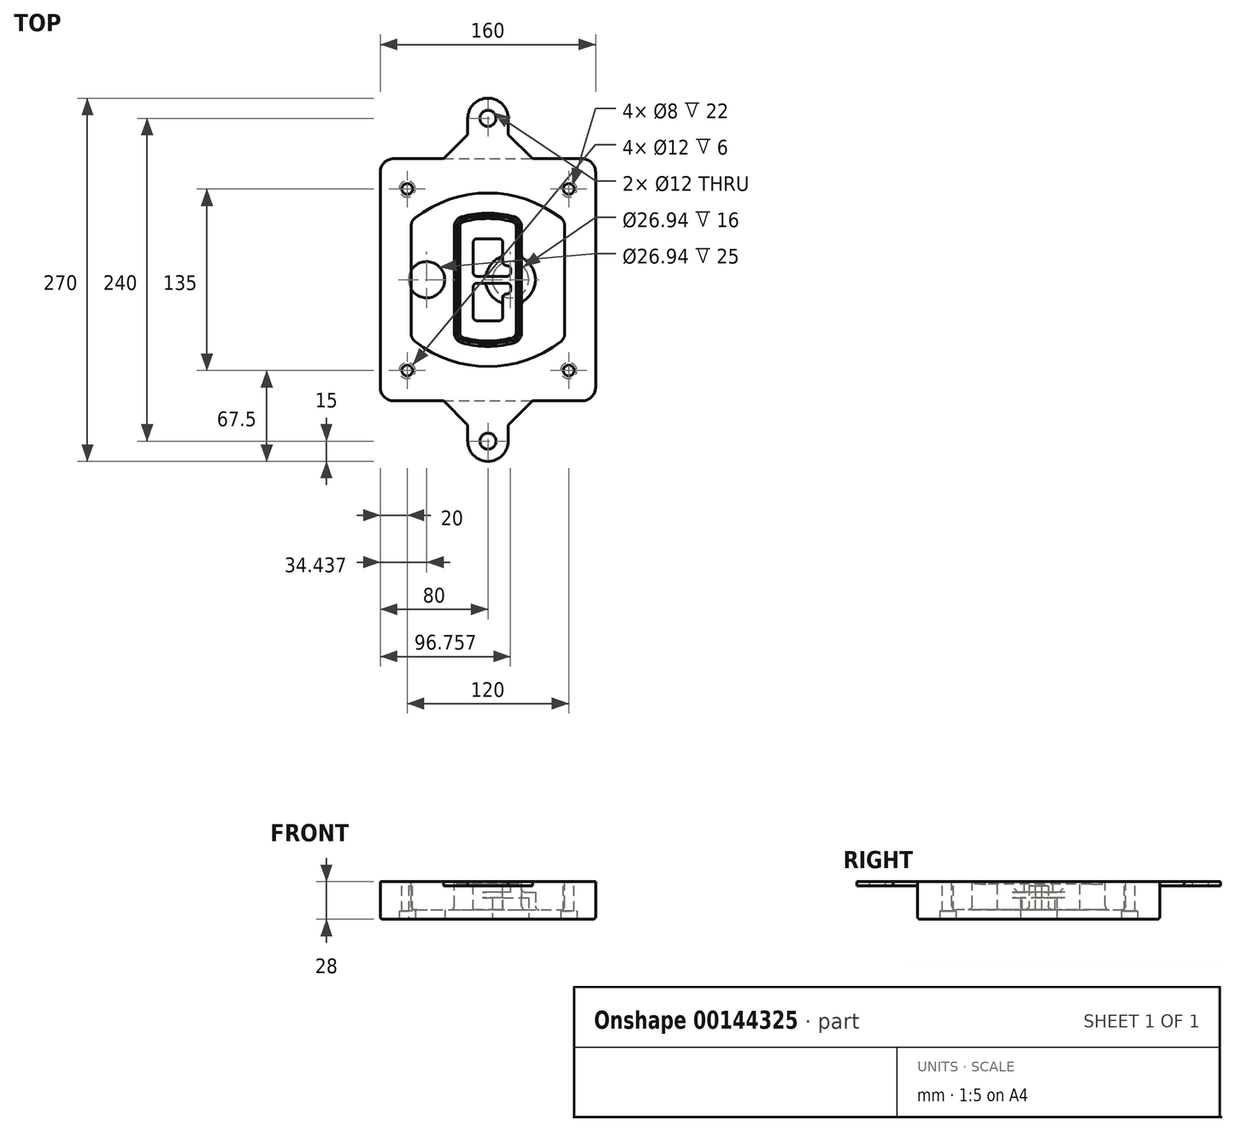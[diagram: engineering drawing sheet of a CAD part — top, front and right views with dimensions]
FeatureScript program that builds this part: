
annotation { "Feature Type Name" : "Feature", "Feature Type Description" : "" }
export const myFeature = defineFeature(function(context is Context, id is Id, definition is map)
    precondition{}
    {
        {
            var Q0;
            Q0=qCreatedBy(makeId("Top.planeOp"),FACE);
            var sketch = newSketch(context, id + "F0", { "sketchPlane" : qUnion([Q0])});
            skPoint(sketch, "E0.rect.middle", {"position": v(0, 0) * mm});
            skLineSegment(sketch, "E1.bottom", {"start": v(-70, -90) * mm, "end": v(70, -90) * mm});
            skLineSegment(sketch, "E1.top", {"start": v(-70, 90) * mm, "end": v(70, 90) * mm});
            skLineSegment(sketch, "E1.left", {"start": v(-80, -80) * mm, "end": v(-80, 80) * mm});
            skLineSegment(sketch, "E1.right", {"start": v(80, -80) * mm, "end": v(80, 80) * mm});
            skLineSegment(sketch, "E2", {"start": v(-80, 90) * mm, "end": v(80, -90) * mm, "construction": true});
            skLineSegment(sketch, "E3", {"start": v(80, 90) * mm, "end": v(-80, -90) * mm, "construction": true});
            skCircle(sketch, "E4", {"center": v(-60, 67.5) * mm, "radius": 4 * mm});
            skCircle(sketch, "E5", {"center": v(60, 67.5) * mm, "radius": 4 * mm});
            skCircle(sketch, "E6", {"center": v(60, -67.5) * mm, "radius": 4 * mm});
            skCircle(sketch, "E7", {"center": v(-60, -67.5) * mm, "radius": 4 * mm});
            skLineSegment(sketch, "E8", {"start": v(-60, 67.5) * mm, "end": v(60, 67.5) * mm, "construction": true});
            skLineSegment(sketch, "E9", {"start": v(60, 67.5) * mm, "end": v(60, -67.5) * mm, "construction": true});
            skLineSegment(sketch, "E10", {"start": v(60, -67.5) * mm, "end": v(-60, -67.5) * mm, "construction": true});
            skLineSegment(sketch, "E11", {"start": v(-60, -67.5) * mm, "end": v(-60, 67.5) * mm, "construction": true});
            skLineSegment(sketch, "E12", {"start": v(-60, 40.3) * mm, "end": v(-60, -40.3) * mm});
            skLineSegment(sketch, "E13", {"start": v(60, 40.3) * mm, "end": v(60, -40.3) * mm});
            skArc(sketch, "E14", {"start": v(56.15, 48.18) * mm, "mid": v(0, 67.5) * mm, "end": v(-56.15, 48.18) * mm});
            skArc(sketch, "E15", {"start": v(-56.15, -48.18) * mm, "mid": v(0, -67.5) * mm, "end": v(56.15, -48.18) * mm});
            skLineSegment(sketch, "E16", {"start": v(-60, 0) * mm, "end": v(60, 0) * mm, "construction": true});
            skPoint(sketch, "E17.visualSharp", {"position": v(-60, -45) * mm});
            skArc(sketch, "E17.filletArc", {"start": v(-60, -40.3) * mm, "mid": v(-58.99, -44.68) * mm, "end": v(-56.15, -48.18) * mm});
            skPoint(sketch, "E18.visualSharp", {"position": v(-60, 45) * mm});
            skArc(sketch, "E18.filletArc", {"start": v(-56.15, 48.18) * mm, "mid": v(-58.99, 44.68) * mm, "end": v(-60, 40.3) * mm});
            skPoint(sketch, "E19.visualSharp", {"position": v(60, 45) * mm});
            skArc(sketch, "E19.filletArc", {"start": v(60, 40.3) * mm, "mid": v(58.99, 44.68) * mm, "end": v(56.15, 48.18) * mm});
            skPoint(sketch, "E20.visualSharp", {"position": v(60, -45) * mm});
            skArc(sketch, "E20.filletArc", {"start": v(56.15, -48.18) * mm, "mid": v(58.99, -44.68) * mm, "end": v(60, -40.3) * mm});
            skPoint(sketch, "E21.visualSharp", {"position": v(-80, 90) * mm});
            skArc(sketch, "E21.filletArc", {"start": v(-70, 90) * mm, "mid": v(-77.07, 87.07) * mm, "end": v(-80, 80) * mm});
            skPoint(sketch, "E22.visualSharp", {"position": v(80, 90) * mm});
            skArc(sketch, "E22.filletArc", {"start": v(80, 80) * mm, "mid": v(77.07, 87.07) * mm, "end": v(70, 90) * mm});
            skPoint(sketch, "E23.visualSharp", {"position": v(80, -90) * mm});
            skArc(sketch, "E23.filletArc", {"start": v(70, -90) * mm, "mid": v(77.07, -87.07) * mm, "end": v(80, -80) * mm});
            skPoint(sketch, "E24.visualSharp", {"position": v(-80, -90) * mm});
            skArc(sketch, "E24.filletArc", {"start": v(-80, -80) * mm, "mid": v(-77.07, -87.07) * mm, "end": v(-70, -90) * mm});
            skArc(sketch, "E25.0", {"start": v(57, 40.3) * mm, "mid": v(56.3, 43.36) * mm, "end": v(54.3, 45.81) * mm});
            skLineSegment(sketch, "E25.1", {"start": v(57, 40.3) * mm, "end": v(57, -40.3) * mm});
            skArc(sketch, "E25.2", {"start": v(54.3, -45.81) * mm, "mid": v(56.3, -43.36) * mm, "end": v(57, -40.3) * mm});
            skArc(sketch, "E25.3", {"start": v(-54.3, -45.81) * mm, "mid": v(0, -64.5) * mm, "end": v(54.3, -45.81) * mm});
            skArc(sketch, "E25.4", {"start": v(-57, -40.3) * mm, "mid": v(-56.3, -43.36) * mm, "end": v(-54.3, -45.81) * mm});
            skArc(sketch, "E25.5", {"start": v(54.3, 45.81) * mm, "mid": v(0, 64.5) * mm, "end": v(-54.3, 45.81) * mm});
            skLineSegment(sketch, "E25.6", {"start": v(-57, 40.3) * mm, "end": v(-57, -40.3) * mm});
            skArc(sketch, "E25.7", {"start": v(-54.3, 45.81) * mm, "mid": v(-56.3, 43.36) * mm, "end": v(-57, 40.3) * mm});
            skArc(sketch, "E26.0", {"start": v(-58.62, 51.33) * mm, "mid": v(-62.58, 46.43) * mm, "end": v(-64, 40.3) * mm});
            skArc(sketch, "E26.1", {"start": v(58.62, 51.33) * mm, "mid": v(0, 71.5) * mm, "end": v(-58.62, 51.33) * mm});
            skArc(sketch, "E26.2", {"start": v(64, 40.3) * mm, "mid": v(62.58, 46.43) * mm, "end": v(58.62, 51.33) * mm});
            skLineSegment(sketch, "E26.3", {"start": v(64, 40.3) * mm, "end": v(64, -40.3) * mm});
            skArc(sketch, "E26.4", {"start": v(58.62, -51.33) * mm, "mid": v(62.58, -46.43) * mm, "end": v(64, -40.3) * mm});
            skLineSegment(sketch, "E26.5", {"start": v(-64, 40.3) * mm, "end": v(-64, -40.3) * mm});
            skArc(sketch, "E26.6", {"start": v(-58.62, -51.33) * mm, "mid": v(0, -71.5) * mm, "end": v(58.62, -51.33) * mm});
            skArc(sketch, "E26.7", {"start": v(-64, -40.3) * mm, "mid": v(-62.58, -46.43) * mm, "end": v(-58.62, -51.33) * mm});
            skSolve(sketch);
        }
        {
            var Q0;
            Q0=makeQuery(id+"F0.imprint","IMPRINT",FACE,{"disambiguationData":[TD([[makeQuery(id+"F0.imprint","IMPRINT",EDGE,{"derivedFrom":sQuery(id+"F0.wireOp",EDGE,"E1.bottom")}),1.0]])]});
            var Q1;
            Q1=makeQuery(id+"F0.imprint","IMPRINT",FACE,{"disambiguationData":[TD([[makeQuery(id+"F0.imprint","IMPRINT",EDGE,{"derivedFrom":sQuery(id+"F0.wireOp",EDGE,"E12")}),1.0]])]});
            var Q2;
            Q2=makeQuery(id+"F0.imprint","IMPRINT",FACE,{"disambiguationData":[TD([[makeQuery(id+"F0.imprint","IMPRINT",EDGE,{"derivedFrom":sQuery(id+"F0.wireOp",EDGE,"E25.0")}),1.0]])]});
            var Q3;
            Q3=makeQuery(id+"F0.imprint","IMPRINT",FACE,{"disambiguationData":[TD([[makeQuery(id+"F0.imprint","IMPRINT",EDGE,{"derivedFrom":sQuery(id+"F0.wireOp",EDGE,"E12")}),-1.0]])]});
            extrude(context, id + "F1", {"entities" : qUnion([Q0, Q1, Q2, Q3]), "oppositeDirection" : true, "depth" : 25 * mm});
        }
        {
            var Q0;
            Q0=makeQuery(id+"F0.imprint","IMPRINT",FACE,{"disambiguationData":[TD([[makeQuery(id+"F0.imprint","IMPRINT",EDGE,{"derivedFrom":sQuery(id+"F0.wireOp",EDGE,"E12")}),1.0]])]});
            extrude(context, id + "F2", {"entities" : qUnion([Q0]), "depth" : 3 * mm});
        }
        {
            var Q0;
            Q0=makeQuery(id+"F0.imprint","IMPRINT",FACE,{"disambiguationData":[TD([[makeQuery(id+"F0.imprint","IMPRINT",EDGE,{"derivedFrom":sQuery(id+"F0.wireOp",EDGE,"E25.0")}),1.0]])]});
            extrude(context, id + "F3", {"entities" : qUnion([Q0]), "operationType" : NewBodyOperationType.REMOVE, "oppositeDirection" : true, "depth" : 18 * mm});
        }
        {
            var Q0;
            Q0=makeQuery(id+"F2.opExtrude","CAP_FACE",FACE,{"disambiguationData":[OSD([sQuery(id+"F0.wireOp",EDGE,"E12"),sQuery(id+"F0.wireOp",EDGE,"E13"),sQuery(id+"F0.wireOp",EDGE,"E14"),sQuery(id+"F0.wireOp",EDGE,"E15"),sQuery(id+"F0.wireOp",EDGE,"E17.filletArc"),sQuery(id+"F0.wireOp",EDGE,"E18.filletArc"),sQuery(id+"F0.wireOp",EDGE,"E19.filletArc"),sQuery(id+"F0.wireOp",EDGE,"E20.filletArc"),sQuery(id+"F0.wireOp",EDGE,"E25.0"),sQuery(id+"F0.wireOp",EDGE,"E25.1"),sQuery(id+"F0.wireOp",EDGE,"E25.2"),sQuery(id+"F0.wireOp",EDGE,"E25.3"),sQuery(id+"F0.wireOp",EDGE,"E25.4"),sQuery(id+"F0.wireOp",EDGE,"E25.5"),sQuery(id+"F0.wireOp",EDGE,"E25.6"),sQuery(id+"F0.wireOp",EDGE,"E25.7")])],"isStart":false});
            var sketch = newSketch(context, id + "F4", { "sketchPlane" : qUnion([Q0])});
            skArc(sketch, "E27.0", {"start": v(-19.08, -46.97) * mm, "mid": v(0, -49.5) * mm, "end": v(19.08, -46.97) * mm});
            skArc(sketch, "E28.0", {"start": v(19.08, 46.97) * mm, "mid": v(0, 49.5) * mm, "end": v(-19.08, 46.97) * mm});
            skLineSegment(sketch, "E29", {"start": v(-25, 39.25) * mm, "end": v(-25, -39.25) * mm});
            skLineSegment(sketch, "E30", {"start": v(25, 39.25) * mm, "end": v(25, -39.25) * mm});
            skLineSegment(sketch, "E31", {"start": v(-25, 45.1) * mm, "end": v(25, 45.1) * mm, "construction": true});
            skLineSegment(sketch, "E32", {"start": v(-25, -45.1) * mm, "end": v(25, -45.1) * mm, "construction": true});
            skPoint(sketch, "E33.visualSharp", {"position": v(-25, 45.1) * mm});
            skArc(sketch, "E33.filletArc", {"start": v(-19.08, 46.97) * mm, "mid": v(-23.35, 44.11) * mm, "end": v(-25, 39.25) * mm});
            skPoint(sketch, "E34.visualSharp", {"position": v(25, 45.1) * mm});
            skArc(sketch, "E34.filletArc", {"start": v(25, 39.25) * mm, "mid": v(23.35, 44.11) * mm, "end": v(19.08, 46.97) * mm});
            skPoint(sketch, "E35.visualSharp", {"position": v(25, -45.1) * mm});
            skArc(sketch, "E35.filletArc", {"start": v(19.08, -46.97) * mm, "mid": v(23.35, -44.11) * mm, "end": v(25, -39.25) * mm});
            skPoint(sketch, "E36.visualSharp", {"position": v(-25, -45.1) * mm});
            skArc(sketch, "E36.filletArc", {"start": v(-25, -39.25) * mm, "mid": v(-23.35, -44.11) * mm, "end": v(-19.08, -46.97) * mm});
            skArc(sketch, "E37.0", {"start": v(54.3, 45.81) * mm, "mid": v(0, 64.5) * mm, "end": v(-54.3, 45.81) * mm});
            skArc(sketch, "E37.1", {"start": v(-54.3, 45.81) * mm, "mid": v(-56.3, 43.36) * mm, "end": v(-57, 40.3) * mm});
            skLineSegment(sketch, "E37.2", {"start": v(-57, 40.3) * mm, "end": v(-57, -40.3) * mm});
            skArc(sketch, "E37.3", {"start": v(-57, -40.3) * mm, "mid": v(-56.3, -43.36) * mm, "end": v(-54.3, -45.81) * mm});
            skArc(sketch, "E37.4", {"start": v(-54.3, -45.81) * mm, "mid": v(0, -64.5) * mm, "end": v(54.3, -45.81) * mm});
            skArc(sketch, "E37.5", {"start": v(54.3, -45.81) * mm, "mid": v(56.3, -43.36) * mm, "end": v(57, -40.3) * mm});
            skLineSegment(sketch, "E37.6", {"start": v(57, 40.3) * mm, "end": v(57, -40.3) * mm});
            skArc(sketch, "E37.7", {"start": v(57, 40.3) * mm, "mid": v(56.3, 43.36) * mm, "end": v(54.3, 45.81) * mm});
            skLineSegment(sketch, "E38.0", {"start": v(23, 39.25) * mm, "end": v(23, -39.25) * mm});
            skArc(sketch, "E38.1", {"start": v(18.56, -45.04) * mm, "mid": v(21.76, -42.9) * mm, "end": v(23, -39.25) * mm});
            skArc(sketch, "E38.2", {"start": v(-18.56, -45.04) * mm, "mid": v(0, -47.5) * mm, "end": v(18.56, -45.04) * mm});
            skArc(sketch, "E38.3", {"start": v(-23, -39.25) * mm, "mid": v(-21.76, -42.9) * mm, "end": v(-18.56, -45.04) * mm});
            skLineSegment(sketch, "E38.4", {"start": v(-23, 39.25) * mm, "end": v(-23, -39.25) * mm});
            skArc(sketch, "E38.5", {"start": v(23, 39.25) * mm, "mid": v(21.76, 42.9) * mm, "end": v(18.56, 45.04) * mm});
            skArc(sketch, "E38.6", {"start": v(-18.56, 45.04) * mm, "mid": v(-21.76, 42.9) * mm, "end": v(-23, 39.25) * mm});
            skArc(sketch, "E38.7", {"start": v(18.56, 45.04) * mm, "mid": v(0, 47.5) * mm, "end": v(-18.56, 45.04) * mm});
            skArc(sketch, "E39.0", {"start": v(21, 39.25) * mm, "mid": v(20.18, 41.68) * mm, "end": v(18.04, 43.1) * mm});
            skLineSegment(sketch, "E39.1", {"start": v(21, 39.25) * mm, "end": v(21, -39.25) * mm});
            skArc(sketch, "E39.2", {"start": v(18.04, -43.1) * mm, "mid": v(20.18, -41.68) * mm, "end": v(21, -39.25) * mm});
            skArc(sketch, "E39.3", {"start": v(-18.04, -43.1) * mm, "mid": v(0, -45.5) * mm, "end": v(18.04, -43.1) * mm});
            skArc(sketch, "E39.4", {"start": v(-21, -39.25) * mm, "mid": v(-20.18, -41.68) * mm, "end": v(-18.04, -43.1) * mm});
            skArc(sketch, "E39.5", {"start": v(18.04, 43.1) * mm, "mid": v(0, 45.5) * mm, "end": v(-18.04, 43.1) * mm});
            skLineSegment(sketch, "E39.6", {"start": v(-21, 39.25) * mm, "end": v(-21, -39.25) * mm});
            skArc(sketch, "E39.7", {"start": v(-18.04, 43.1) * mm, "mid": v(-20.18, 41.68) * mm, "end": v(-21, 39.25) * mm});
            skLineSegment(sketch, "E40", {"start": v(-25, 0) * mm, "end": v(25, 0) * mm, "construction": true});
            skLineSegment(sketch, "E41", {"start": v(-11, 5.5) * mm, "end": v(-11, 27.5) * mm});
            skLineSegment(sketch, "E42", {"start": v(-8, 30.5) * mm, "end": v(8, 30.5) * mm});
            skLineSegment(sketch, "E43", {"start": v(11, 27.5) * mm, "end": v(11, 13.5) * mm});
            skLineSegment(sketch, "E44", {"start": v(14, 10.5) * mm, "end": v(14, 10.5) * mm});
            skLineSegment(sketch, "E45", {"start": v(17, 7.5) * mm, "end": v(17, 5.5) * mm});
            skLineSegment(sketch, "E46", {"start": v(14, 2.5) * mm, "end": v(-8, 2.5) * mm});
            skPoint(sketch, "E47.visualSharp", {"position": v(-11, 30.5) * mm});
            skArc(sketch, "E47.filletArc", {"start": v(-8, 30.5) * mm, "mid": v(-10.12, 29.62) * mm, "end": v(-11, 27.5) * mm});
            skPoint(sketch, "E48.visualSharp", {"position": v(11, 30.5) * mm});
            skArc(sketch, "E48.filletArc", {"start": v(11, 27.5) * mm, "mid": v(10.12, 29.62) * mm, "end": v(8, 30.5) * mm});
            skPoint(sketch, "E49.visualSharp", {"position": v(11, 10.5) * mm});
            skArc(sketch, "E49.filletArc", {"start": v(11, 13.5) * mm, "mid": v(11.88, 11.38) * mm, "end": v(14, 10.5) * mm});
            skPoint(sketch, "E50.visualSharp", {"position": v(17, 10.5) * mm});
            skArc(sketch, "E50.filletArc", {"start": v(17, 7.5) * mm, "mid": v(16.12, 9.62) * mm, "end": v(14, 10.5) * mm});
            skPoint(sketch, "E51.visualSharp", {"position": v(17, 2.5) * mm});
            skArc(sketch, "E51.filletArc", {"start": v(14, 2.5) * mm, "mid": v(16.12, 3.38) * mm, "end": v(17, 5.5) * mm});
            skPoint(sketch, "E52.visualSharp", {"position": v(-11, 2.5) * mm});
            skArc(sketch, "E52.filletArc", {"start": v(-11, 5.5) * mm, "mid": v(-10.12, 3.38) * mm, "end": v(-8, 2.5) * mm});
            skLineSegment(sketch, "E53.0.MirrorCS", {"start": v(14, -2.5) * mm, "end": v(-8, -2.5) * mm});
            skArc(sketch, "E54.0.MirrorCS", {"start": v(-11, -5.5) * mm, "mid": v(-10.12, -3.38) * mm, "end": v(-8, -2.5) * mm});
            skLineSegment(sketch, "E55.0.MirrorCS", {"start": v(-11, -5.5) * mm, "end": v(-11, -27.5) * mm});
            skArc(sketch, "E56.0.MirrorCS", {"start": v(-8, -30.5) * mm, "mid": v(-10.12, -29.62) * mm, "end": v(-11, -27.5) * mm});
            skLineSegment(sketch, "E57.0.MirrorCS", {"start": v(-8, -30.5) * mm, "end": v(8, -30.5) * mm});
            skArc(sketch, "E58.0.MirrorCS", {"start": v(11, -27.5) * mm, "mid": v(10.12, -29.62) * mm, "end": v(8, -30.5) * mm});
            skLineSegment(sketch, "E59.0.MirrorCS", {"start": v(11, -27.5) * mm, "end": v(11, -13.5) * mm});
            skArc(sketch, "E60.0.MirrorCS", {"start": v(11, -13.5) * mm, "mid": v(11.88, -11.38) * mm, "end": v(14, -10.5) * mm});
            skArc(sketch, "E61.0.MirrorCS", {"start": v(17, -7.5) * mm, "mid": v(16.12, -9.62) * mm, "end": v(14, -10.5) * mm});
            skLineSegment(sketch, "E62.0.MirrorCS", {"start": v(17, -7.5) * mm, "end": v(17, -5.5) * mm});
            skArc(sketch, "E63.0.MirrorCS", {"start": v(14, -2.5) * mm, "mid": v(16.12, -3.38) * mm, "end": v(17, -5.5) * mm});
            skSolve(sketch);
        }
        {
            var Q0;
            Q0=makeQuery(id+"F4.imprint","IMPRINT",FACE,{"disambiguationData":[TD([[makeQuery(id+"F4.imprint","IMPRINT",EDGE,{"derivedFrom":sQuery(id+"F4.wireOp",EDGE,"E27.0")}),1.0]])]});
            var Q1;
            Q1=makeQuery(id+"F4.imprint","IMPRINT",FACE,{"disambiguationData":[TD([[makeQuery(id+"F4.imprint","IMPRINT",EDGE,{"derivedFrom":sQuery(id+"F4.wireOp",EDGE,"E38.0")}),-1.0]])]});
            var Q2;
            Q2=makeQuery(id+"F4.imprint","IMPRINT",FACE,{"disambiguationData":[TD([[makeQuery(id+"F4.imprint","IMPRINT",EDGE,{"derivedFrom":sQuery(id+"F4.wireOp",EDGE,"E39.0")}),1.0]])]});
            extrude(context, id + "F5", {"entities" : qUnion([Q0, Q1, Q2]), "operationType" : NewBodyOperationType.ADD, "endBound" : BoundingType.UP_TO_NEXT, "oppositeDirection" : true, "depth" : 25 * mm});
        }
        {
            var Q0;
            Q0=makeQuery(id+"F4.imprint","IMPRINT",FACE,{"disambiguationData":[TD([[makeQuery(id+"F4.imprint","IMPRINT",EDGE,{"derivedFrom":sQuery(id+"F4.wireOp",EDGE,"E38.0")}),-1.0]])]});
            extrude(context, id + "F6", {"entities" : qUnion([Q0]), "operationType" : NewBodyOperationType.REMOVE, "oppositeDirection" : true, "depth" : 2 * mm});
        }
        {
            var Q0;
            Q0=makeQuery(id+"F1.opExtrude","CAP_FACE",FACE,{"disambiguationData":[OSD([sQuery(id+"F0.wireOp",EDGE,"E1.bottom"),sQuery(id+"F0.wireOp",EDGE,"E1.top"),sQuery(id+"F0.wireOp",EDGE,"E1.left"),sQuery(id+"F0.wireOp",EDGE,"E1.right"),sQuery(id+"F0.wireOp",EDGE,"E4"),sQuery(id+"F0.wireOp",EDGE,"E5"),sQuery(id+"F0.wireOp",EDGE,"E6"),sQuery(id+"F0.wireOp",EDGE,"E7"),sQuery(id+"F0.wireOp",EDGE,"E21.filletArc"),sQuery(id+"F0.wireOp",EDGE,"E22.filletArc"),sQuery(id+"F0.wireOp",EDGE,"E23.filletArc"),sQuery(id+"F0.wireOp",EDGE,"E24.filletArc")])],"isStart":false});
            var sketch = newSketch(context, id + "F7", { "sketchPlane" : qUnion([Q0])});
            skCircle(sketch, "E64", {"center": v(16.76, 0) * mm, "radius": 13.47 * mm});
            skCircle(sketch, "E65", {"center": v(-45.56, 0) * mm, "radius": 13.47 * mm});
            skLineSegment(sketch, "E66", {"start": v(80, 0) * mm, "end": v(-80, 0) * mm});
            skCircle(sketch, "E67", {"center": v(16.76, 0) * mm, "radius": 18.47 * mm});
            skCircle(sketch, "E68", {"center": v(60, -67.5) * mm, "radius": 6 * mm});
            skCircle(sketch, "E69", {"center": v(-60, -67.5) * mm, "radius": 6 * mm});
            skCircle(sketch, "E70", {"center": v(-60, 67.5) * mm, "radius": 6 * mm});
            skCircle(sketch, "E71", {"center": v(60, 67.5) * mm, "radius": 6 * mm});
            skSolve(sketch);
        }
        {
            var Q0;
            {var subQ1=sQuery(id+"F7.wireOp",EDGE,"E66");var subQ4=sQuery(id+"F7.wireOp",EDGE,"E64");var subQ6=makeQuery(id+"F7.imprint","INTERSECT",VERTEX,{"disambiguationData":[OD(0.0)],"derivedFrom":[subQ4,subQ1]});Q0=makeQuery(id+"F7.imprint","IMPRINT",FACE,{"disambiguationData":[TD([[makeQuery(id+"F7.imprint","IMPRINT",EDGE,{"disambiguationData":[TD([[subQ6,-1.0]])],"derivedFrom":subQ4}),-1.0]])]});}
            var Q1;
            {var subQ0=sQuery(id+"F7.wireOp",EDGE,"E66");var subQ1=sQuery(id+"F7.wireOp",EDGE,"E64");var subQ3=makeQuery(id+"F7.imprint","INTERSECT",VERTEX,{"disambiguationData":[OD(0.0)],"derivedFrom":[subQ1,subQ0]});Q1=makeQuery(id+"F7.imprint","IMPRINT",FACE,{"disambiguationData":[TD([[makeQuery(id+"F7.imprint","IMPRINT",EDGE,{"disambiguationData":[TD([[subQ3,-1.0]])],"derivedFrom":subQ1}),1.0]])]});}
            var Q2;
            {var subQ0=sQuery(id+"F7.wireOp",EDGE,"E66");var subQ1=sQuery(id+"F7.wireOp",EDGE,"E64");var subQ3=makeQuery(id+"F7.imprint","INTERSECT",VERTEX,{"disambiguationData":[OD(0.0)],"derivedFrom":[subQ1,subQ0]});Q2=makeQuery(id+"F7.imprint","IMPRINT",FACE,{"disambiguationData":[TD([[makeQuery(id+"F7.imprint","IMPRINT",EDGE,{"disambiguationData":[TD([[subQ3,1.0]])],"derivedFrom":subQ1}),1.0]])]});}
            var Q3;
            {var subQ1=sQuery(id+"F7.wireOp",EDGE,"E66");var subQ4=sQuery(id+"F7.wireOp",EDGE,"E64");var subQ6=makeQuery(id+"F7.imprint","INTERSECT",VERTEX,{"disambiguationData":[OD(0.0)],"derivedFrom":[subQ4,subQ1]});Q3=makeQuery(id+"F7.imprint","IMPRINT",FACE,{"disambiguationData":[TD([[makeQuery(id+"F7.imprint","IMPRINT",EDGE,{"disambiguationData":[TD([[subQ6,1.0]])],"derivedFrom":subQ4}),-1.0]])]});}
            extrude(context, id + "F8", {"entities" : qUnion([Q0, Q1, Q2, Q3]), "operationType" : NewBodyOperationType.ADD, "oppositeDirection" : true, "depth" : 20 * mm});
        }
        {
            var Q0;
            {var subQ0=sQuery(id+"F7.wireOp",EDGE,"E66");var subQ1=sQuery(id+"F7.wireOp",EDGE,"E64");var subQ3=makeQuery(id+"F7.imprint","INTERSECT",VERTEX,{"disambiguationData":[OD(0.0)],"derivedFrom":[subQ1,subQ0]});Q0=makeQuery(id+"F7.imprint","IMPRINT",FACE,{"disambiguationData":[TD([[makeQuery(id+"F7.imprint","IMPRINT",EDGE,{"disambiguationData":[TD([[subQ3,-1.0]])],"derivedFrom":subQ1}),1.0]])]});}
            var Q1;
            {var subQ0=sQuery(id+"F7.wireOp",EDGE,"E66");var subQ1=sQuery(id+"F7.wireOp",EDGE,"E64");var subQ3=makeQuery(id+"F7.imprint","INTERSECT",VERTEX,{"disambiguationData":[OD(0.0)],"derivedFrom":[subQ1,subQ0]});Q1=makeQuery(id+"F7.imprint","IMPRINT",FACE,{"disambiguationData":[TD([[makeQuery(id+"F7.imprint","IMPRINT",EDGE,{"disambiguationData":[TD([[subQ3,1.0]])],"derivedFrom":subQ1}),1.0]])]});}
            extrude(context, id + "F9", {"entities" : qUnion([Q0, Q1]), "operationType" : NewBodyOperationType.REMOVE, "oppositeDirection" : true, "depth" : 16 * mm});
        }
        {
            var Q0;
            {var subQ0=sQuery(id+"F7.wireOp",EDGE,"E66");var subQ1=sQuery(id+"F7.wireOp",EDGE,"E65");var subQ3=makeQuery(id+"F7.imprint","INTERSECT",VERTEX,{"disambiguationData":[OD(0.0)],"derivedFrom":[subQ1,subQ0]});Q0=makeQuery(id+"F7.imprint","IMPRINT",FACE,{"disambiguationData":[TD([[makeQuery(id+"F7.imprint","IMPRINT",EDGE,{"disambiguationData":[TD([[subQ3,-1.0]])],"derivedFrom":subQ1}),1.0]])]});}
            var Q1;
            {var subQ0=sQuery(id+"F7.wireOp",EDGE,"E66");var subQ1=sQuery(id+"F7.wireOp",EDGE,"E65");var subQ3=makeQuery(id+"F7.imprint","INTERSECT",VERTEX,{"disambiguationData":[OD(0.0)],"derivedFrom":[subQ1,subQ0]});Q1=makeQuery(id+"F7.imprint","IMPRINT",FACE,{"disambiguationData":[TD([[makeQuery(id+"F7.imprint","IMPRINT",EDGE,{"disambiguationData":[TD([[subQ3,1.0]])],"derivedFrom":subQ1}),1.0]])]});}
            extrude(context, id + "F10", {"entities" : qUnion([Q0, Q1]), "operationType" : NewBodyOperationType.REMOVE, "oppositeDirection" : true, "depth" : 25 * mm});
        }
        {
            var Q0;
            Q0=makeQuery(id+"F7.imprint","IMPRINT",FACE,{"disambiguationData":[TD([[makeQuery(id+"F7.imprint","IMPRINT",EDGE,{"derivedFrom":sQuery(id+"F7.wireOp",EDGE,"E68")}),1.0]])]});
            var Q1;
            Q1=makeQuery(id+"F7.imprint","IMPRINT",FACE,{"disambiguationData":[TD([[makeQuery(id+"F7.imprint","IMPRINT",EDGE,{"derivedFrom":makeQuery(id+"F1.opExtrude","CAP_EDGE",EDGE,{"disambiguationData":[OSD([sQuery(id+"F0.wireOp",EDGE,"E5")])],"isStart":false})}),-1.0]])]});
            var Q2;
            Q2=makeQuery(id+"F7.imprint","IMPRINT",FACE,{"disambiguationData":[TD([[makeQuery(id+"F7.imprint","IMPRINT",EDGE,{"derivedFrom":sQuery(id+"F7.wireOp",EDGE,"E69")}),1.0]])]});
            var Q3;
            Q3=makeQuery(id+"F7.imprint","IMPRINT",FACE,{"disambiguationData":[TD([[makeQuery(id+"F7.imprint","IMPRINT",EDGE,{"derivedFrom":makeQuery(id+"F1.opExtrude","CAP_EDGE",EDGE,{"disambiguationData":[OSD([sQuery(id+"F0.wireOp",EDGE,"E4")])],"isStart":false})}),-1.0]])]});
            var Q4;
            Q4=makeQuery(id+"F7.imprint","IMPRINT",FACE,{"disambiguationData":[TD([[makeQuery(id+"F7.imprint","IMPRINT",EDGE,{"derivedFrom":sQuery(id+"F7.wireOp",EDGE,"E70")}),1.0]])]});
            var Q5;
            Q5=makeQuery(id+"F7.imprint","IMPRINT",FACE,{"disambiguationData":[TD([[makeQuery(id+"F7.imprint","IMPRINT",EDGE,{"derivedFrom":makeQuery(id+"F1.opExtrude","CAP_EDGE",EDGE,{"disambiguationData":[OSD([sQuery(id+"F0.wireOp",EDGE,"E7")])],"isStart":false})}),-1.0]])]});
            var Q6;
            Q6=makeQuery(id+"F7.imprint","IMPRINT",FACE,{"disambiguationData":[TD([[makeQuery(id+"F7.imprint","IMPRINT",EDGE,{"derivedFrom":sQuery(id+"F7.wireOp",EDGE,"E71")}),1.0]])]});
            var Q7;
            Q7=makeQuery(id+"F7.imprint","IMPRINT",FACE,{"disambiguationData":[TD([[makeQuery(id+"F7.imprint","IMPRINT",EDGE,{"derivedFrom":makeQuery(id+"F1.opExtrude","CAP_EDGE",EDGE,{"disambiguationData":[OSD([sQuery(id+"F0.wireOp",EDGE,"E6")])],"isStart":false})}),-1.0]])]});
            extrude(context, id + "F11", {"entities" : qUnion([Q0, Q1, Q2, Q3, Q4, Q5, Q6, Q7]), "operationType" : NewBodyOperationType.REMOVE, "oppositeDirection" : true, "depth" : 6 * mm});
        }
        {
            var Q0;
            Q0=makeQuery(id+"F9.boolean.opBoolean","COPY",FACE,{"derivedFrom":makeQuery(id+"F9.opExtrude","CAP_FACE",FACE,{"disambiguationData":[OSD([sQuery(id+"F7.wireOp",EDGE,"E64")])],"isStart":false})});
            var sketch = newSketch(context, id + "F12", { "sketchPlane" : qUnion([Q0])});
            skArc(sketch, "E72.0", {"start": v(11, 17.55) * mm, "mid": v(2.57, 11.82) * mm, "end": v(-1.54, 2.5) * mm});
            skArc(sketch, "E72.1", {"start": v(-1.54, -2.5) * mm, "mid": v(2.57, -11.82) * mm, "end": v(11, -17.55) * mm});
            skLineSegment(sketch, "E73", {"start": v(-1.54, -2.5) * mm, "end": v(14, -2.5) * mm});
            skLineSegment(sketch, "E74.0", {"start": v(14, 2.5) * mm, "end": v(-1.54, 2.5) * mm});
            skArc(sketch, "E74.1", {"start": v(14, 2.5) * mm, "mid": v(16.12, 3.38) * mm, "end": v(17, 5.5) * mm});
            skLineSegment(sketch, "E74.2", {"start": v(17, 7.5) * mm, "end": v(17, 5.5) * mm});
            skArc(sketch, "E74.3", {"start": v(17, 7.5) * mm, "mid": v(16.12, 9.62) * mm, "end": v(14, 10.5) * mm});
            skArc(sketch, "E74.4", {"start": v(11, 13.5) * mm, "mid": v(11.88, 11.38) * mm, "end": v(14, 10.5) * mm});
            skLineSegment(sketch, "E74.5", {"start": v(11, 17.55) * mm, "end": v(11, 13.5) * mm});
            skLineSegment(sketch, "E74.7", {"start": v(14, -2.5) * mm, "end": v(-1.54, -2.5) * mm});
            skArc(sketch, "E74.8", {"start": v(14, -2.5) * mm, "mid": v(16.12, -3.38) * mm, "end": v(17, -5.5) * mm});
            skLineSegment(sketch, "E74.9", {"start": v(17, -7.5) * mm, "end": v(17, -5.5) * mm});
            skArc(sketch, "E74.10", {"start": v(17, -7.5) * mm, "mid": v(16.12, -9.62) * mm, "end": v(14, -10.5) * mm});
            skArc(sketch, "E74.11", {"start": v(11, -13.5) * mm, "mid": v(11.88, -11.38) * mm, "end": v(14, -10.5) * mm});
            skLineSegment(sketch, "E74.12", {"start": v(11, -17.55) * mm, "end": v(11, -13.5) * mm});
            skPoint(sketch, "E75.orphan", {"position": v(11, -27.5) * mm});
            skPoint(sketch, "E76.orphan", {"position": v(-8, -2.5) * mm});
            skPoint(sketch, "E77.orphan", {"position": v(-8, 2.5) * mm});
            skPoint(sketch, "E78.orphan", {"position": v(11, 27.5) * mm});
            skSolve(sketch);
        }
        {
            var Q0;
            {var subQ7=sQuery(id+"F12.wireOp",EDGE,"E72.0");var subQ14=sQuery(id+"F12.wireOp",EDGE,"E72.1");var subQ16=sQuery(id+"F12.wireOp",EDGE,"E74.1");var subQ18=sQuery(id+"F12.wireOp",EDGE,"E74.8");Q0=qUnion([makeQuery(id+"F12.imprint","IMPRINT",FACE,{"disambiguationData":[TD([[makeQuery(id+"F12.imprint","IMPRINT",EDGE,{"derivedFrom":subQ7}),1.0]])]}),makeQuery(id+"F12.imprint","IMPRINT",FACE,{"disambiguationData":[TD([[makeQuery(id+"F12.imprint","IMPRINT",EDGE,{"derivedFrom":subQ14}),1.0]])]}),makeQuery(id+"F12.imprint","IMPRINT",FACE,{"disambiguationData":[TD([[makeQuery(id+"F12.imprint","IMPRINT",EDGE,{"derivedFrom":subQ16}),1.0]])]}),makeQuery(id+"F12.imprint","IMPRINT",FACE,{"disambiguationData":[TD([[makeQuery(id+"F12.imprint","IMPRINT",EDGE,{"derivedFrom":subQ18}),-1.0]])]})]);}
            var Q1;
            Q1=makeQuery(id+"F5.boolean.opBoolean","SPLIT",FACE,{"disambiguationData":[TD([makeQuery(id+"F5.opExtrude","SWEPT_FACE",FACE,{"disambiguationData":[OSD([sQuery(id+"F4.wireOp",EDGE,"E41")])]})])],"derivedFrom":makeQuery(id+"F3.boolean.opBoolean","COPY",FACE,{"derivedFrom":makeQuery(id+"F3.opExtrude","CAP_FACE",FACE,{"disambiguationData":[OSD([sQuery(id+"F0.wireOp",EDGE,"E25.0"),sQuery(id+"F0.wireOp",EDGE,"E25.1"),sQuery(id+"F0.wireOp",EDGE,"E25.2"),sQuery(id+"F0.wireOp",EDGE,"E25.3"),sQuery(id+"F0.wireOp",EDGE,"E25.4"),sQuery(id+"F0.wireOp",EDGE,"E25.5"),sQuery(id+"F0.wireOp",EDGE,"E25.6"),sQuery(id+"F0.wireOp",EDGE,"E25.7")])],"isStart":false})})});
            extrude(context, id + "F13", {"entities" : qUnion([Q0]), "operationType" : NewBodyOperationType.REMOVE, "endBound" : BoundingType.UP_TO_SURFACE, "endBoundEntityFace" : qUnion([Q1]), "depth" : 25 * mm});
        }
        {
            var Q0;
            Q0=makeQuery(id+"F3.boolean.opBoolean","COPY",EDGE,{"derivedFrom":makeQuery(id+"F3.opExtrude","CAP_EDGE",EDGE,{"disambiguationData":[OSD([sQuery(id+"F0.wireOp",EDGE,"E25.6")])],"isStart":false})});
            var Q1;
            Q1=makeQuery(id+"F8.boolean.opBoolean","INTERSECT",EDGE,{"derivedFrom":[makeQuery(id+"F5.opExtrude","SWEPT_FACE",FACE,{"disambiguationData":[OSD([sQuery(id+"F4.wireOp",EDGE,"E30")])]}),makeQuery(id+"F8.opExtrude","CAP_FACE",FACE,{"disambiguationData":[OSD([sQuery(id+"F7.wireOp",EDGE,"E67")])],"isStart":false})]});
            var Q2;
            Q2=makeQuery(id+"F8.boolean.opBoolean","INTERSECT",EDGE,{"disambiguationData":[OD(1.0)],"derivedFrom":[makeQuery(id+"F5.opExtrude","SWEPT_FACE",FACE,{"disambiguationData":[OSD([sQuery(id+"F4.wireOp",EDGE,"E30")])]}),makeQuery(id+"F8.opExtrude","SWEPT_FACE",FACE,{"disambiguationData":[OSD([sQuery(id+"F7.wireOp",EDGE,"E67")])]})]});
            var Q3;
            {var subQ0=sQuery(id+"F4.wireOp",EDGE,"E30");Q3=makeQuery(id+"F8.boolean.opBoolean","SPLIT",EDGE,{"disambiguationData":[TD([makeQuery(id+"F5.opExtrude","SWEPT_FACE",FACE,{"disambiguationData":[OSD([sQuery(id+"F4.wireOp",EDGE,"E35.filletArc")])]})])],"derivedFrom":makeQuery(id+"F5.opExtrude","CAP_EDGE",EDGE,{"disambiguationData":[OSD([subQ0])],"isStart":false})});}
            var Q4;
            {var subQ0=makeQuery(id+"F8.opExtrude","SWEPT_FACE",FACE,{"disambiguationData":[OSD([sQuery(id+"F7.wireOp",EDGE,"E67")])]});var subQ1=makeQuery(id+"F5.opExtrude","SWEPT_FACE",FACE,{"disambiguationData":[OSD([sQuery(id+"F4.wireOp",EDGE,"E30")])]});var subQ2=sQuery(id+"F0.wireOp",EDGE,"E25.3");var subQ3=sQuery(id+"F0.wireOp",EDGE,"E25.7");var subQ4=sQuery(id+"F0.wireOp",EDGE,"E25.6");var subQ5=sQuery(id+"F0.wireOp",EDGE,"E25.5");var subQ6=sQuery(id+"F0.wireOp",EDGE,"E25.4");var subQ7=sQuery(id+"F0.wireOp",EDGE,"E25.0");var subQ8=sQuery(id+"F0.wireOp",EDGE,"E25.1");var subQ9=sQuery(id+"F0.wireOp",EDGE,"E25.2");Q4=qUnion([makeQuery(id+"F8.boolean.opBoolean","INTERSECT",EDGE,{"derivedFrom":[makeQuery(id+"F5.boolean.opBoolean","SPLIT",FACE,{"disambiguationData":[TD([makeQuery(id+"F3.boolean.opBoolean","COPY",FACE,{"derivedFrom":makeQuery(id+"F3.opExtrude","SWEPT_FACE",FACE,{"disambiguationData":[OSD([subQ7])]})})])],"derivedFrom":makeQuery(id+"F3.boolean.opBoolean","COPY",FACE,{"derivedFrom":makeQuery(id+"F3.opExtrude","CAP_FACE",FACE,{"disambiguationData":[OSD([subQ7,subQ8,subQ9,subQ2,subQ6,subQ5,subQ4,subQ3])],"isStart":false})})}),subQ0]}),makeQuery(id+"F8.boolean.opBoolean","INTERSECT",EDGE,{"derivedFrom":[makeQuery(id+"F5.opExtrude","SWEPT_FACE",FACE,{"disambiguationData":[OSD([sQuery(id+"F4.wireOp",EDGE,"E53.0.MirrorCS")])]}),subQ0]}),makeQuery(id+"F8.boolean.opBoolean","INTERSECT",EDGE,{"derivedFrom":[makeQuery(id+"F5.opExtrude","SWEPT_FACE",FACE,{"disambiguationData":[OSD([sQuery(id+"F4.wireOp",EDGE,"E46")])]}),subQ0]}),makeQuery(id+"F8.boolean.opBoolean","INTERSECT",EDGE,{"disambiguationData":[OD(1.0)],"derivedFrom":[subQ1,subQ0]}),makeQuery(id+"F8.boolean.opBoolean","INTERSECT",EDGE,{"derivedFrom":[makeQuery(id+"F5.opExtrude","SWEPT_FACE",FACE,{"disambiguationData":[OSD([sQuery(id+"F4.wireOp",EDGE,"E43")])]}),subQ0]}),makeQuery(id+"F8.boolean.opBoolean","INTERSECT",EDGE,{"disambiguationData":[OD(0.0)],"derivedFrom":[subQ1,subQ0]}),makeQuery(id+"F8.boolean.opBoolean","INTERSECT",EDGE,{"derivedFrom":[makeQuery(id+"F5.opExtrude","SWEPT_FACE",FACE,{"disambiguationData":[OSD([sQuery(id+"F4.wireOp",EDGE,"E59.0.MirrorCS")])]}),subQ0]})]);}
            var Q5;
            Q5=makeQuery(id+"F8.boolean.opBoolean","INTERSECT",EDGE,{"disambiguationData":[OD(0.0)],"derivedFrom":[makeQuery(id+"F5.opExtrude","SWEPT_FACE",FACE,{"disambiguationData":[OSD([sQuery(id+"F4.wireOp",EDGE,"E30")])]}),makeQuery(id+"F8.opExtrude","SWEPT_FACE",FACE,{"disambiguationData":[OSD([sQuery(id+"F7.wireOp",EDGE,"E67")])]})]});
            fillet(context, id + "F14", {"entities" : qUnion([Q0, Q1, Q2, Q3, Q4, Q5]), "radius" : 3 * mm, "tangentPropagation" : true, "allowEdgeOverflow" : false});
        }
        {
            var Q0;
            Q0=makeQuery(id+"F1.opExtrude","CAP_EDGE",EDGE,{"disambiguationData":[OSD([sQuery(id+"F0.wireOp",EDGE,"E1.bottom")])],"isStart":false});
            fillet(context, id + "F15", {"entities" : qUnion([Q0]), "radius" : 2 * mm, "tangentPropagation" : true, "allowEdgeOverflow" : false});
        }
        {
            var Q0;
            {var subQ0=sQuery(id+"F0.wireOp",EDGE,"E22.filletArc");var subQ1=sQuery(id+"F0.wireOp",EDGE,"E7");var subQ2=sQuery(id+"F0.wireOp",EDGE,"E6");var subQ3=sQuery(id+"F0.wireOp",EDGE,"E5");var subQ4=sQuery(id+"F0.wireOp",EDGE,"E4");var subQ5=sQuery(id+"F0.wireOp",EDGE,"E1.bottom");var subQ6=sQuery(id+"F0.wireOp",EDGE,"E21.filletArc");var subQ7=sQuery(id+"F0.wireOp",EDGE,"E1.top");var subQ8=sQuery(id+"F0.wireOp",EDGE,"E1.left");var subQ9=sQuery(id+"F0.wireOp",EDGE,"E1.right");var subQ10=sQuery(id+"F0.wireOp",EDGE,"E23.filletArc");var subQ11=sQuery(id+"F0.wireOp",EDGE,"E24.filletArc");Q0=makeQuery(id+"F2.boolean.opBoolean","SPLIT",FACE,{"disambiguationData":[TD([makeQuery(id+"F1.opExtrude","SWEPT_FACE",FACE,{"disambiguationData":[OSD([subQ5])]})])],"derivedFrom":makeQuery(id+"F1.opExtrude","CAP_FACE",FACE,{"disambiguationData":[OSD([subQ5,subQ7,subQ8,subQ9,subQ4,subQ3,subQ2,subQ1,subQ6,subQ0,subQ10,subQ11])],"isStart":true})});}
            var sketch = newSketch(context, id + "F16", { "sketchPlane" : qUnion([Q0])});
            skLineSegment(sketch, "E79", {"start": v(0, 90) * mm, "end": v(0, 120) * mm, "construction": true});
            skLineSegment(sketch, "E80", {"start": v(-33, 90) * mm, "end": v(-15, 108) * mm});
            skLineSegment(sketch, "E81", {"start": v(-15, 108) * mm, "end": v(-15, 120) * mm});
            skLineSegment(sketch, "E82", {"start": v(33, 90) * mm, "end": v(15, 108) * mm});
            skLineSegment(sketch, "E83", {"start": v(15, 108) * mm, "end": v(15, 120) * mm});
            skCircle(sketch, "E84", {"center": v(0, 120) * mm, "radius": 6 * mm});
            skArc(sketch, "E85", {"start": v(15, 120) * mm, "mid": v(0, 135) * mm, "end": v(-15, 120) * mm});
            skLineSegment(sketch, "E86", {"start": v(-80, 0) * mm, "end": v(80, 0) * mm, "construction": true});
            skLineSegment(sketch, "E87.MirrorCS", {"start": v(0, -90) * mm, "end": v(0, -120) * mm, "construction": true});
            skLineSegment(sketch, "E88.MirrorCS", {"start": v(-33, -90) * mm, "end": v(-15, -108) * mm});
            skLineSegment(sketch, "E89.MirrorCS", {"start": v(-15, -108) * mm, "end": v(-15, -120) * mm});
            skCircle(sketch, "E90.MirrorC", {"center": v(0, -120) * mm, "radius": 6 * mm});
            skArc(sketch, "E91.MirrorCS", {"start": v(15, -120) * mm, "mid": v(0, -135) * mm, "end": v(-15, -120) * mm});
            skLineSegment(sketch, "E92.MirrorCS", {"start": v(15, -108) * mm, "end": v(15, -120) * mm});
            skLineSegment(sketch, "E93.MirrorCS", {"start": v(33, -90) * mm, "end": v(15, -108) * mm});
            skSolve(sketch);
        }
        {
            var Q0;
            {var subQ0=sQuery(id+"F16.wireOp",EDGE,"E88.MirrorCS");Q0=makeQuery(id+"F16.imprint","IMPRINT",FACE,{"disambiguationData":[TD([[makeQuery(id+"F16.imprint","IMPRINT",EDGE,{"derivedFrom":subQ0}),1.0]])]});}
            var Q1;
            {var subQ1=sQuery(id+"F16.wireOp",EDGE,"E80");Q1=makeQuery(id+"F16.imprint","IMPRINT",FACE,{"disambiguationData":[TD([[makeQuery(id+"F16.imprint","IMPRINT",EDGE,{"derivedFrom":subQ1}),-1.0]])]});}
            var Q2;
            Q2=makeQuery(id+"F16.imprint","IMPRINT",FACE,{"disambiguationData":[TD([[makeQuery(id+"F16.imprint","IMPRINT",EDGE,{"derivedFrom":makeQuery(id+"F1.opExtrude","CAP_EDGE",EDGE,{"disambiguationData":[OSD([sQuery(id+"F0.wireOp",EDGE,"E1.left")])],"isStart":true})}),-1.0]])]});
            var Q3;
            Q3=makeQuery(id+"F2.opExtrude","CAP_FACE",FACE,{"disambiguationData":[OSD([sQuery(id+"F0.wireOp",EDGE,"E12"),sQuery(id+"F0.wireOp",EDGE,"E13"),sQuery(id+"F0.wireOp",EDGE,"E14"),sQuery(id+"F0.wireOp",EDGE,"E15"),sQuery(id+"F0.wireOp",EDGE,"E17.filletArc"),sQuery(id+"F0.wireOp",EDGE,"E18.filletArc"),sQuery(id+"F0.wireOp",EDGE,"E19.filletArc"),sQuery(id+"F0.wireOp",EDGE,"E20.filletArc"),sQuery(id+"F0.wireOp",EDGE,"E25.0"),sQuery(id+"F0.wireOp",EDGE,"E25.1"),sQuery(id+"F0.wireOp",EDGE,"E25.2"),sQuery(id+"F0.wireOp",EDGE,"E25.3"),sQuery(id+"F0.wireOp",EDGE,"E25.4"),sQuery(id+"F0.wireOp",EDGE,"E25.5"),sQuery(id+"F0.wireOp",EDGE,"E25.6"),sQuery(id+"F0.wireOp",EDGE,"E25.7")])],"isStart":false});
            extrude(context, id + "F17", {"entities" : qUnion([Q0, Q1, Q2]), "operationType" : NewBodyOperationType.ADD, "endBound" : BoundingType.UP_TO_SURFACE, "endBoundEntityFace" : qUnion([Q3]), "depth" : 25 * mm});
        }
    });
